# Revit family: ONHM-NRG
name_source: partatom
category: Mechanical Equipment
units: mm (PartAtom-declared; Revit-internal decimal feet)

## family parameters
Always vertical = Yes
Cut with Voids When Loaded = No
OmniClass Number = 23.40.40.11.17
OmniClass Title = Refrigerated Cases
Part Type = Normal
Room Calculation Point = No
Round Connector Dimension = Use Radius
Shared = No
Work Plane-Based = Yes

## types (12) — shared parameters
12" Shelf = Yes
14" Shelf = Yes
16" Shelf = Yes
18" Shelf = Yes
20" Shelf = Yes
BOTTOM ELECTRICAL = Yes
BOTTOM REFRIGERATION PIPING = Yes
Certifications = NSF 7, UL471, CSA
DATE = 06/17/2020
DESIGNERS NAME = T.A.G
DRAIN PIPING = Yes
Default Elevation = 48"
Defrosts Per Day = 6
Description = Narrow Multi-Deck Merchandiser
Discharge Air (°F) = 30 °F
Discharge Air Velocity (FPM) = 220 FPM
EQUIPMENT DESCRIPTION = Narrow Multi-Deck Merchandiser
EQUIPMENT MARK = ONHM
Evaporator (°F) = 26 °F
Front Options = Utility Multi-Deck Dynamic 11in Front : O2 6" Thermopane Front
GLASS = Glass
Height = 75 1/8"
High Efficiency Amps = 1 A
Item Description = Narrow Multi-Deck Merchandiser
LF STD END = Yes
Legend Number = ONHM
Manufacturer = HILL PHOENIX
Model = ONHM
PAINTED METAL UPPER SHELF = PAINTED SHELVES
REAR REFRIGERATION PIPING = Yes
REFRIGERATION PIPING = COPPER PIPE
RT STD END = Yes
STAINLESS STEEL = GALVANIZED STEEL
Standard Power Amps = 0 A
Superheat Set Point @ Bulb (°F) = 6-8 °F
TOP ELECTRICAL = Yes
TOP REFRIGERATION PIPING = Yes
Timed-Off Defrost Fail-Safe (Min) = 40 (Min)
Timed-Off Defrost Termination Temp = 42 °F
URL = http://www.hillphoenix.com
Width = 35 7/8"

## per-type parameters (varying)
| type | Application Discipline | BTUH Conventional | BTUH Parallel | CENTER LINE | Front Sill Height | High Efficiency Watts | High Power (Cornice) Amps | High Power (Cornice) Watts | Length | Length of Cases | Light Length | Lights Per Row | Number of Fans | Refgn | Standard Power Watts | Type of Case |
| 04' All Other Front Sill Heights | All Other Front Sill Heights | 1450 | 1345 | 72" | Standard | 72 W | 0 A | 45 W | 144" | 48" | 4' | 3 | 4 | 7 5/8" | 18 W |  |
| 06' All Other Front Sill Heights | All Other Front Sill Heights | 1450 | 1345 | 36" | Standard | 54 W | 0 A | 30 W | 72" | 72" | 3' | 2 | 3 | 8 5/8" | 17 W | All Others |
| 08' All Other Front Sill Heights | All Other Front Sill Heights | 1450 | 1345 | 48" | Standard | 54 W | 0 A | 43 W | 96" | 96" | 4' | 2 | 3 | 8 5/8" | 24 W | All Others |
| 12' All Other Front Sill Heights | All Other Front Sill Heights | 1450 | 1345 | 72" | Standard | 72 W | 1 A | 65 W | 144" | 144" | 4' | 3 | 4 | 8 5/8" | 36 W | All Others |
| 04' Standard Front Sill Height | Standard Front Sill Height | 1550 | 1450 | 24" | Standard | 36 W | 0 A | 22 W | 48" | 48" | 4' | 1 | 2 | 7 5/8" | 12 W |  |
| 06' Standard Front Sill Height | Standard Front Sill Height | 1550 | 1450 | 36" | Standard | 54 W | 0 A | 30 W | 72" | 72" | 3' | 2 | 3 | 8 5/8" | 17 W |  |
| 08' Standard Front Sill Height | Standard Front Sill Height | 1550 | 1450 | 48" | Standard | 54 W | 0 A | 43 W | 96" | 96" | 4' | 2 | 3 | 8 5/8" | 24 W |  |
| 12' Standard Front Sill Height | Standard Front Sill Height | 1550 | 1450 | 72" | Standard | 72 W | 1 A | 65 W | 144" | 144" | 4' | 3 | 4 | 8 5/8" | 36 W |  |
| 12' | All Other Front Sill Heights | 1450 | 1345 | 72" | Standard | 72 W | 0 A | 45 W | 144" | 48" | 4' | 3 | 4 | 7 5/8" | 18 W |  |
| 8' | All Other Front Sill Heights | 1450 | 1345 | 48" | Standard | 54 W | 0 A | 30 W | 96" | 48" | 4' | 2 | 3 | 8 5/8" | 12 W |  |
| 6' | All Other Front Sill Heights | 1450 | 1345 | 36" | All others | 54 W | 0 A | 24 W | 72" | 48" | 3' | 2 | 3 | 8 5/8" | 9 W |  |
| 4' | All Other Front Sill Heights | 1550 | 1450 | 24" | Standard | 36 W | 0 A | 15 W | 48" | 48" | 4' | 1 | 2 | 7 5/8" | 6 W |  |

## geometry (parser evidence)
native form markers: Blend x13, Sweep x30
no freeform markers — native parametric forms only
